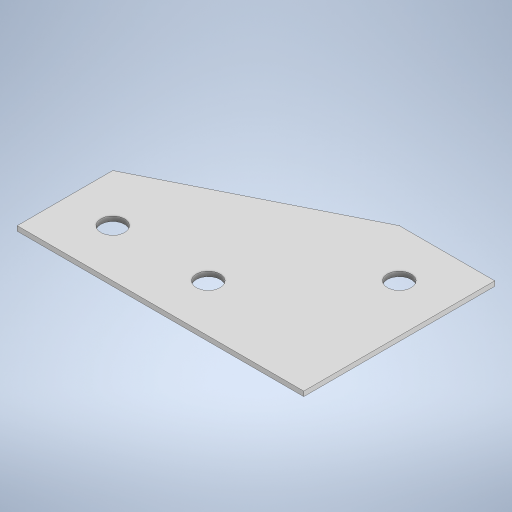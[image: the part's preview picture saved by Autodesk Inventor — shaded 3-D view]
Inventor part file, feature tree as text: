
AUTODESK INVENTOR PART (.ipt)
format: ipt  version: 2023 (Build 270158000, 158)  size: 228,352 bytes
history: native  units: mm
features: other x1, extrude x1, sketch x1
ambient origin geometry x8: Origin, YZ Plane, XZ Plane, XY Plane, X Axis, Y Axis, Z Axis, Center Point
bodies: Body1 (feature_tree)
feature tree (3):
  other  "Твердое тело1"
  extrude  "Выдавливание1"  Depth=80.0mm
  sketch  "Эскиз1"
